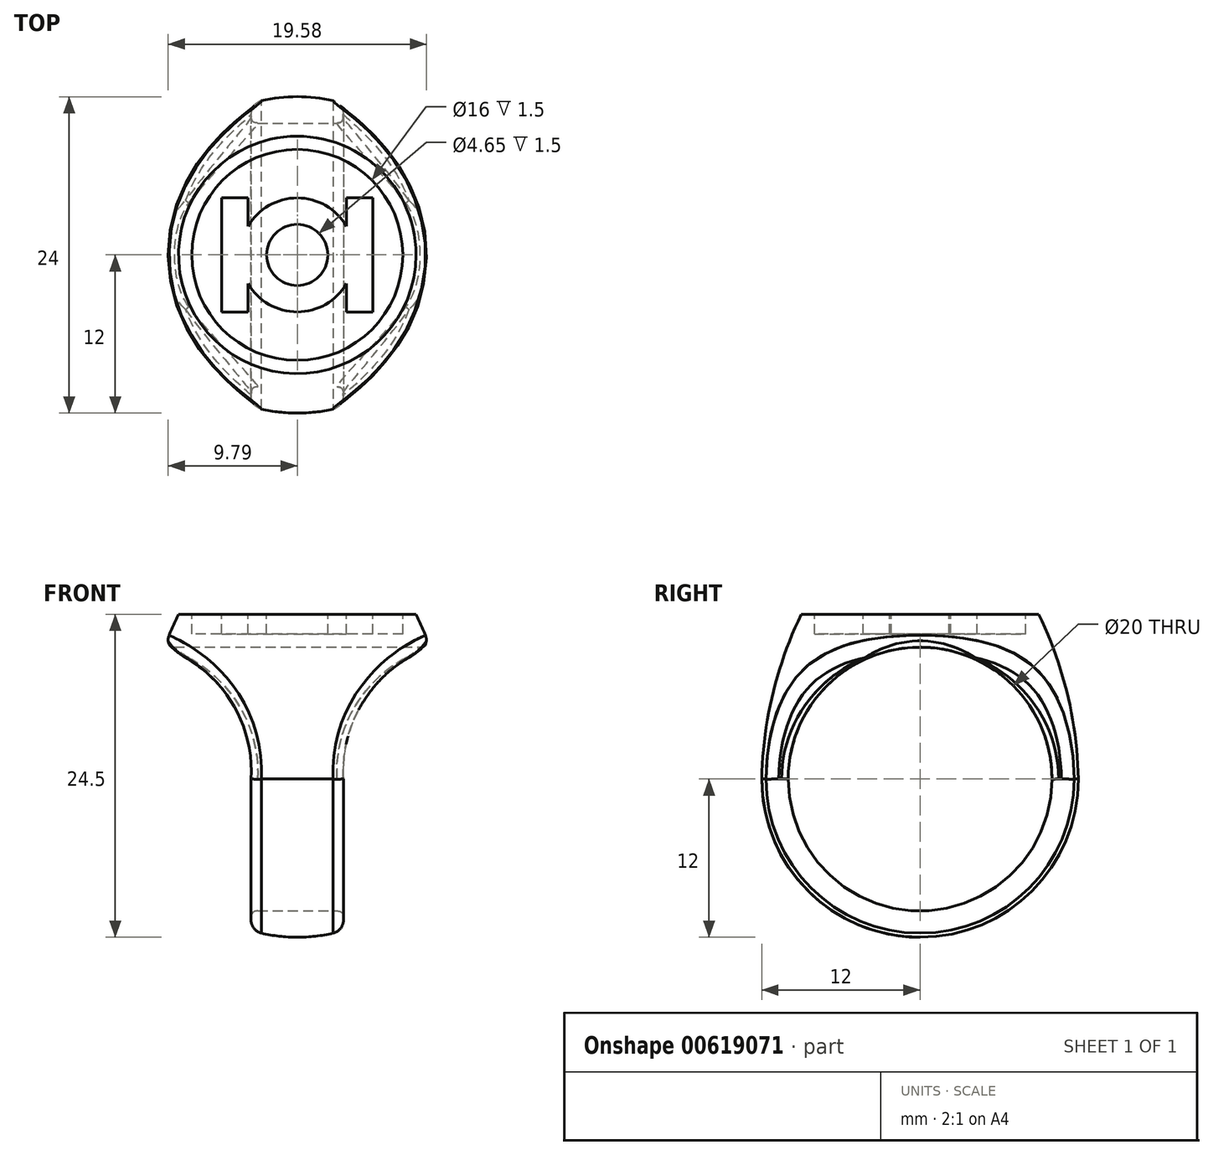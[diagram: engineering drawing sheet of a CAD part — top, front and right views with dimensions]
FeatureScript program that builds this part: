
annotation { "Feature Type Name" : "Feature", "Feature Type Description" : "" }
export const myFeature = defineFeature(function(context is Context, id is Id, definition is map)
    precondition{}
    {
        {
            var Q0;
            Q0=qCreatedBy(makeId("Right.planeOp"),FACE);
            var sketch = newSketch(context, id + "F0", { "sketchPlane" : qUnion([Q0])});
            skLineSegment(sketch, "E0", {"start": v(0, 0) * mm, "end": v(0, -24.5) * mm});
            skLineSegment(sketch, "E1", {"start": v(0, 0) * mm, "end": v(-9, 0) * mm});
            skArc(sketch, "E2", {"start": v(-12, -12.5) * mm, "mid": v(-8.49, -20.99) * mm, "end": v(0, -24.5) * mm});
            skLineSegment(sketch, "E3", {"start": v(0, -12.5) * mm, "end": v(-12, -12.5) * mm, "construction": true});
            skArc(sketch, "E4", {"start": v(-9, 0) * mm, "mid": v(-11.18, -6.09) * mm, "end": v(-12, -12.5) * mm});
            skSolve(sketch);
        }
        {
            var Q0;
            Q0=makeQuery(id+"F0.imprint","IMPRINT",FACE,{"disambiguationData":[TD([[makeQuery(id+"F0.imprint","IMPRINT",EDGE,{"derivedFrom":sQuery(id+"F0.wireOp",EDGE,"E0")}),-1.0]])]});
            var Q1;
            Q1=sQuery(id+"F0.wireOp",EDGE,"E0");
            revolve(context, id + "F1", {"entities" : qUnion([Q0]), "axis" : qUnion([Q1]), "revolveType" : RevolveType.FULL});
        }
        {
            var Q0;
            Q0=qCreatedBy(makeId("Right.planeOp"),FACE);
            var sketch = newSketch(context, id + "F2", { "sketchPlane" : qUnion([Q0])});
            skCircle(sketch, "E5", {"center": v(0, -12.5) * mm, "radius": 10 * mm});
            skSolve(sketch);
        }
        {
            var Q0;
            Q0=qSketchRegion(id+"F2",true);
            extrude(context, id + "F3", {"entities" : qUnion([Q0]), "operationType" : NewBodyOperationType.REMOVE, "endBound" : BoundingType.SYMMETRIC, "oppositeDirection" : true, "depth" : 25 * mm, "offsetDistance" : 25 * mm});
        }
        {
            var Q0;
            Q0=qCreatedBy(makeId("Front.planeOp"),FACE);
            var sketch = newSketch(context, id + "F4", { "sketchPlane" : qUnion([Q0])});
            skLineSegment(sketch, "E6", {"start": v(3.5, -26.5) * mm, "end": v(3.5, -12.5) * mm});
            skArc(sketch, "E7", {"start": v(10.15, -2.5) * mm, "mid": v(5.16, -6.39) * mm, "end": v(3.5, -12.5) * mm});
            skLineSegment(sketch, "E8", {"start": v(10.15, -2.5) * mm, "end": v(11.65, -2.5) * mm});
            skLineSegment(sketch, "E9", {"start": v(11.65, -2.5) * mm, "end": v(11.65, -26.5) * mm});
            skLineSegment(sketch, "E10", {"start": v(11.65, -26.5) * mm, "end": v(3.5, -26.5) * mm});
            skPoint(sketch, "E11.start.orphan", {"position": v(0, -24.5) * mm});
            skLineSegment(sketch, "E12", {"start": v(0, 0) * mm, "end": v(0, -24.5) * mm, "construction": true});
            skLineSegment(sketch, "E13.MirrorCS", {"start": v(-3.5, -26.5) * mm, "end": v(-3.5, -12.5) * mm});
            skArc(sketch, "E14.MirrorCS", {"start": v(-10.15, -2.5) * mm, "mid": v(-5.16, -6.39) * mm, "end": v(-3.5, -12.5) * mm});
            skLineSegment(sketch, "E15.MirrorCS", {"start": v(-11.65, -2.5) * mm, "end": v(-11.65, -26.5) * mm});
            skLineSegment(sketch, "E16.MirrorCS", {"start": v(-11.65, -26.5) * mm, "end": v(-3.5, -26.5) * mm});
            skLineSegment(sketch, "E17.MirrorCS", {"start": v(-10.15, -2.5) * mm, "end": v(-11.65, -2.5) * mm});
            skSolve(sketch);
        }
        {
            var Q0;
            Q0=qSketchRegion(id+"F4",true);
            extrude(context, id + "F5", {"entities" : qUnion([Q0]), "operationType" : NewBodyOperationType.REMOVE, "endBound" : BoundingType.SYMMETRIC, "depth" : 25 * mm, "offsetDistance" : 25 * mm});
        }
        {
            var Q0;
            Q0=makeQuery(id+"F1.opRevolve","SWEPT_FACE",FACE,{"disambiguationData":[OSD([sQuery(id+"F0.wireOp",EDGE,"E1")])]});
            var sketch = newSketch(context, id + "F6", { "sketchPlane" : qUnion([Q0])});
            skCircle(sketch, "E18", {"center": v(0, 0) * mm, "radius": 8 * mm});
            skLineSegment(sketch, "E19", {"start": v(-8, 0) * mm, "end": v(8, 0) * mm, "construction": true});
            skArc(sketch, "E20", {"start": v(-3.73, -2.18) * mm, "mid": v(0, -4.32) * mm, "end": v(3.73, -2.18) * mm});
            skLineSegment(sketch, "E21", {"start": v(-6.73, -4.32) * mm, "end": v(6.73, -4.32) * mm, "construction": true});
            skLineSegment(sketch, "E22", {"start": v(-6.73, 4.32) * mm, "end": v(6.73, 4.32) * mm, "construction": true});
            skCircle(sketch, "E23", {"center": v(0, 0) * mm, "radius": 2.32 * mm});
            skLineSegment(sketch, "E24.bottom", {"start": v(5.73, 4.32) * mm, "end": v(3.73, 4.32) * mm});
            skLineSegment(sketch, "E24.top", {"start": v(5.73, -4.32) * mm, "end": v(3.73, -4.32) * mm});
            skLineSegment(sketch, "E24.left", {"start": v(5.73, 4.32) * mm, "end": v(5.73, -4.32) * mm});
            skLineSegment(sketch, "E24.right", {"start": v(3.73, 4.32) * mm, "end": v(3.73, 2.18) * mm});
            skLineSegment(sketch, "E25.bottom", {"start": v(-5.73, 4.32) * mm, "end": v(-3.73, 4.32) * mm});
            skLineSegment(sketch, "E25.top", {"start": v(-5.73, -4.32) * mm, "end": v(-3.73, -4.32) * mm});
            skLineSegment(sketch, "E25.left", {"start": v(-5.73, 4.32) * mm, "end": v(-5.73, -4.32) * mm});
            skLineSegment(sketch, "E25.right", {"start": v(-3.73, 4.32) * mm, "end": v(-3.73, 2.18) * mm});
            skLineSegment(sketch, "E26.trimOffspring", {"start": v(-3.73, 0) * mm, "end": v(-3.73, -4.32) * mm});
            skArc(sketch, "E27.trimOffspring", {"start": v(3.73, 2.18) * mm, "mid": v(0, 4.32) * mm, "end": v(-3.73, 2.18) * mm});
            skLineSegment(sketch, "E28.trimOffspring", {"start": v(3.73, -2.18) * mm, "end": v(3.73, -4.32) * mm});
            skSolve(sketch);
        }
        {
            var Q0;
            Q0=qSketchRegion(id+"F6",true);
            var Q1;
            Q1=makeQuery(id+"F6.imprint","IMPRINT",FACE,{"disambiguationData":[TD([[makeQuery(id+"F6.imprint","IMPRINT",EDGE,{"derivedFrom":sQuery(id+"F6.wireOp",EDGE,"E23")}),1.0]])]});
            extrude(context, id + "F7", {"entities" : qUnion([Q0, Q1]), "operationType" : NewBodyOperationType.REMOVE, "oppositeDirection" : true, "depth" : 1.5 * mm, "offsetDistance" : 25 * mm});
        }
        {
            var Q0;
            Q0=makeQuery(id+"F5.boolean.opBoolean","INTERSECT",EDGE,{"disambiguationData":[OD(1.0)],"derivedFrom":[makeQuery(id+"F1.opRevolve","SWEPT_FACE",FACE,{"disambiguationData":[OSD([sQuery(id+"F0.wireOp",EDGE,"E4")])]}),makeQuery(id+"F5.opExtrude","SWEPT_FACE",FACE,{"disambiguationData":[OSD([sQuery(id+"F4.wireOp",EDGE,"E14.MirrorCS")])]})]});
            var Q1;
            Q1=makeQuery(id+"F5.boolean.opBoolean","INTERSECT",EDGE,{"derivedFrom":[makeQuery(id+"F1.opRevolve","SWEPT_FACE",FACE,{"disambiguationData":[OSD([sQuery(id+"F0.wireOp",EDGE,"E2")])]}),makeQuery(id+"F5.opExtrude","SWEPT_FACE",FACE,{"disambiguationData":[OSD([sQuery(id+"F4.wireOp",EDGE,"E13.MirrorCS")])]})]});
            var Q2;
            Q2=makeQuery(id+"F5.boolean.opBoolean","INTERSECT",EDGE,{"disambiguationData":[OD(1.0)],"derivedFrom":[makeQuery(id+"F1.opRevolve","SWEPT_FACE",FACE,{"disambiguationData":[OSD([sQuery(id+"F0.wireOp",EDGE,"E4")])]}),makeQuery(id+"F5.opExtrude","SWEPT_FACE",FACE,{"disambiguationData":[OSD([sQuery(id+"F4.wireOp",EDGE,"E7")])]})]});
            var Q3;
            Q3=makeQuery(id+"F5.boolean.opBoolean","INTERSECT",EDGE,{"derivedFrom":[makeQuery(id+"F1.opRevolve","SWEPT_FACE",FACE,{"disambiguationData":[OSD([sQuery(id+"F0.wireOp",EDGE,"E2")])]}),makeQuery(id+"F5.opExtrude","SWEPT_FACE",FACE,{"disambiguationData":[OSD([sQuery(id+"F4.wireOp",EDGE,"E6")])]})]});
            fillet(context, id + "F8", {"entities" : qUnion([Q0, Q1, Q2, Q3]), "radius" : 1 * mm, "allowEdgeOverflow" : false});
        }
        {
            var Q0;
            Q0=makeQuery(id+"F5.boolean.opBoolean","INTERSECT",EDGE,{"disambiguationData":[OD(1.0)],"derivedFrom":[makeQuery(id+"F3.boolean.opBoolean","COPY",FACE,{"derivedFrom":makeQuery(id+"F3.opExtrude","SWEPT_FACE",FACE,{"disambiguationData":[OSD([sQuery(id+"F2.wireOp",EDGE,"E5")])]})}),makeQuery(id+"F5.opExtrude","SWEPT_FACE",FACE,{"disambiguationData":[OSD([sQuery(id+"F4.wireOp",EDGE,"E14.MirrorCS")])]})]});
            var Q1;
            Q1=makeQuery(id+"F5.boolean.opBoolean","INTERSECT",EDGE,{"derivedFrom":[makeQuery(id+"F3.boolean.opBoolean","COPY",FACE,{"derivedFrom":makeQuery(id+"F3.opExtrude","SWEPT_FACE",FACE,{"disambiguationData":[OSD([sQuery(id+"F2.wireOp",EDGE,"E5")])]})}),makeQuery(id+"F5.opExtrude","SWEPT_FACE",FACE,{"disambiguationData":[OSD([sQuery(id+"F4.wireOp",EDGE,"E13.MirrorCS")])]})]});
            var Q2;
            Q2=makeQuery(id+"F5.boolean.opBoolean","INTERSECT",EDGE,{"disambiguationData":[OD(0.0)],"derivedFrom":[makeQuery(id+"F3.boolean.opBoolean","COPY",FACE,{"derivedFrom":makeQuery(id+"F3.opExtrude","SWEPT_FACE",FACE,{"disambiguationData":[OSD([sQuery(id+"F2.wireOp",EDGE,"E5")])]})}),makeQuery(id+"F5.opExtrude","SWEPT_FACE",FACE,{"disambiguationData":[OSD([sQuery(id+"F4.wireOp",EDGE,"E14.MirrorCS")])]})]});
            var Q3;
            Q3=makeQuery(id+"F5.boolean.opBoolean","INTERSECT",EDGE,{"disambiguationData":[OD(0.0)],"derivedFrom":[makeQuery(id+"F3.boolean.opBoolean","COPY",FACE,{"derivedFrom":makeQuery(id+"F3.opExtrude","SWEPT_FACE",FACE,{"disambiguationData":[OSD([sQuery(id+"F2.wireOp",EDGE,"E5")])]})}),makeQuery(id+"F5.opExtrude","SWEPT_FACE",FACE,{"disambiguationData":[OSD([sQuery(id+"F4.wireOp",EDGE,"E7")])]})]});
            var Q4;
            Q4=makeQuery(id+"F3.boolean.opBoolean","COPY",FACE,{"derivedFrom":makeQuery(id+"F3.opExtrude","SWEPT_FACE",FACE,{"disambiguationData":[OSD([sQuery(id+"F2.wireOp",EDGE,"E5")])]})});
            fillet(context, id + "F9", {"entities" : qUnion([Q0, Q1, Q2, Q3, Q4]), "radius" : .5 * mm, "rho" : 0.5, "crossSection" : FilletCrossSection.CONIC, "allowEdgeOverflow" : false});
        }
    });
